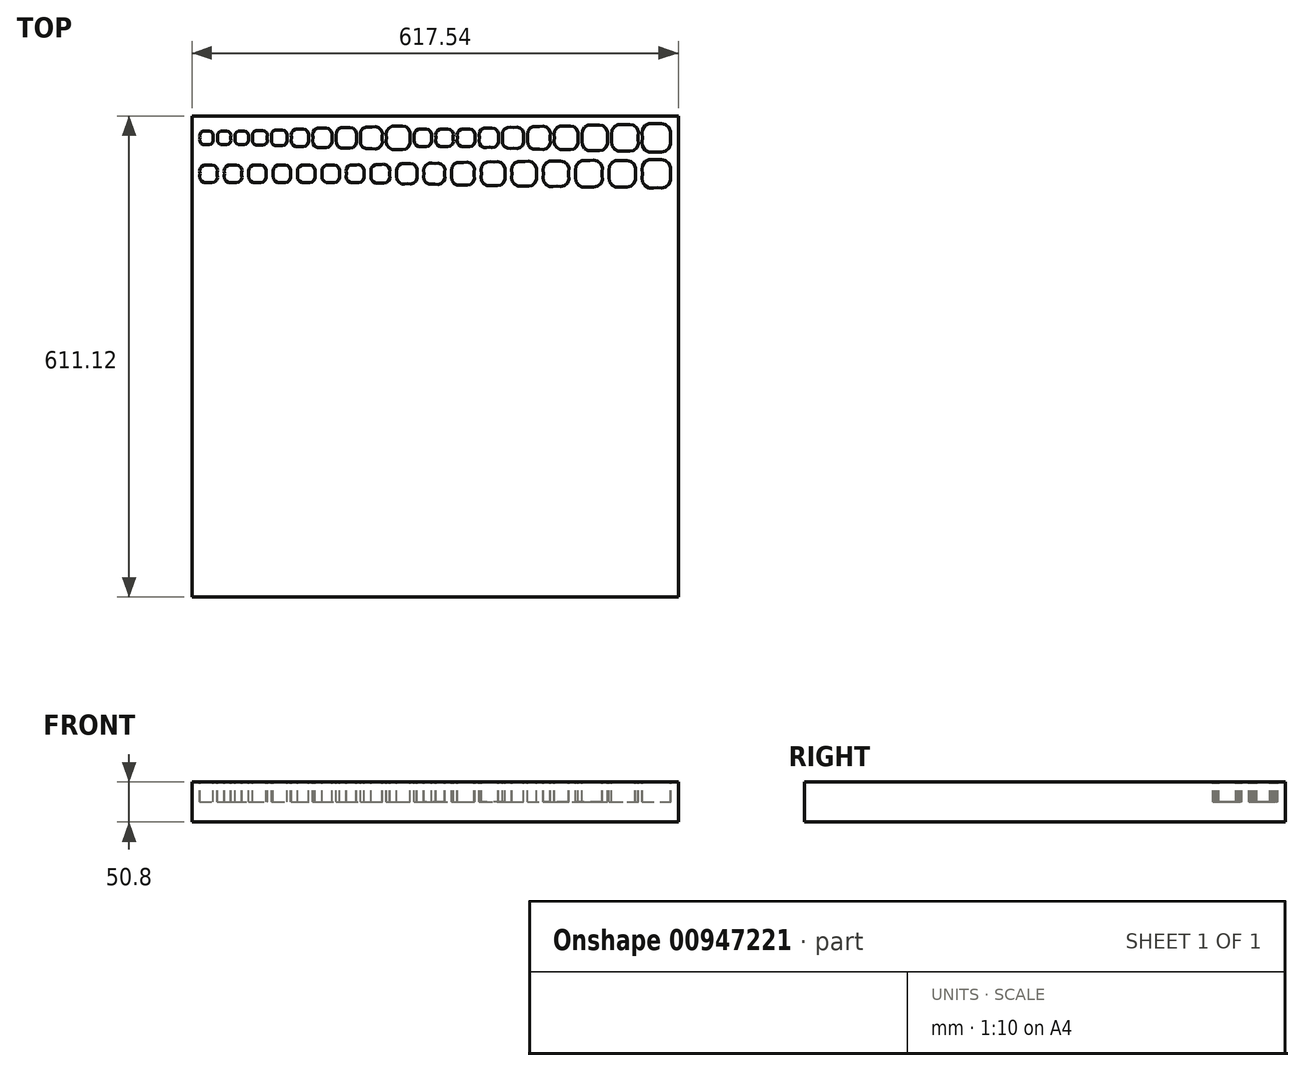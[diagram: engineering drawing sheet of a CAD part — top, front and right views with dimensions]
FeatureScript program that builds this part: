
annotation { "Feature Type Name" : "Feature", "Feature Type Description" : "" }
export const myFeature = defineFeature(function(context is Context, id is Id, definition is map)
    precondition{}
    {
        {
            var Q0;
            Q0=qCreatedBy(makeId("Top.planeOp"),FACE);
            var sketch = newSketch(context, id + "F0", { "sketchPlane" : qUnion([Q0])});
            skLineSegment(sketch, "E0", {"start": v(308.77, -305.56) * mm, "end": v(-308.77, -305.56) * mm});
            skLineSegment(sketch, "E1", {"start": v(-308.77, -305.56) * mm, "end": v(-308.77, 305.56) * mm});
            skLineSegment(sketch, "E2", {"start": v(-308.77, 305.56) * mm, "end": v(308.77, 305.56) * mm});
            skLineSegment(sketch, "E3", {"start": v(308.77, 305.56) * mm, "end": v(308.77, -305.56) * mm});
            skFitSpline(sketch, "E4", {"points": [v(263.12, 277.74) * mm, v(263.12, 287.58) * mm, v(271.1, 295.56) * mm, v(280.94, 295.56) * mm, v(290.79, 295.56) * mm, v(298.77, 287.58) * mm, v(298.77, 277.74) * mm, v(298.77, 267.9) * mm, v(290.79, 259.91) * mm, v(280.94, 259.91) * mm, v(271.1, 259.91) * mm, v(263.12, 267.9) * mm, v(263.12, 277.74) * mm]});
            skFitSpline(sketch, "E5", {"points": [v(224.2, 277.74) * mm, v(224.2, 286.96) * mm, v(231.68, 294.44) * mm, v(240.9, 294.44) * mm, v(250.13, 294.44) * mm, v(257.6, 286.96) * mm, v(257.6, 277.74) * mm, v(257.6, 268.51) * mm, v(250.13, 261.03) * mm, v(240.9, 261.03) * mm, v(231.68, 261.03) * mm, v(224.2, 268.51) * mm, v(224.2, 277.74) * mm]});
            skFitSpline(sketch, "E6", {"points": [v(186.67, 277.74) * mm, v(186.67, 286.58) * mm, v(193.84, 293.75) * mm, v(202.68, 293.75) * mm, v(211.52, 293.75) * mm, v(218.69, 286.58) * mm, v(218.69, 277.74) * mm, v(218.69, 268.9) * mm, v(211.52, 261.73) * mm, v(202.68, 261.73) * mm, v(193.84, 261.73) * mm, v(186.67, 268.9) * mm, v(186.67, 277.74) * mm]});
            skFitSpline(sketch, "E7", {"points": [v(151.47, 277.74) * mm, v(151.47, 285.94) * mm, v(158.12, 292.58) * mm, v(166.31, 292.58) * mm, v(174.51, 292.58) * mm, v(181.16, 285.94) * mm, v(181.16, 277.74) * mm, v(181.16, 269.54) * mm, v(174.51, 262.9) * mm, v(166.31, 262.9) * mm, v(158.12, 262.9) * mm, v(151.47, 269.54) * mm, v(151.47, 277.74) * mm]});
            skFitSpline(sketch, "E8", {"points": [v(117.43, 277.74) * mm, v(117.43, 285.62) * mm, v(123.82, 292) * mm, v(131.7, 292) * mm, v(139.57, 292) * mm, v(145.96, 285.62) * mm, v(145.96, 277.74) * mm, v(145.96, 269.86) * mm, v(139.57, 263.47) * mm, v(131.7, 263.47) * mm, v(123.82, 263.47) * mm, v(117.43, 269.86) * mm, v(117.43, 277.74) * mm]});
            skFitSpline(sketch, "E9", {"points": [v(85.64, 277.74) * mm, v(85.64, 285) * mm, v(91.52, 290.88) * mm, v(98.78, 290.88) * mm, v(106.04, 290.88) * mm, v(111.92, 285) * mm, v(111.92, 277.74) * mm, v(111.92, 270.48) * mm, v(106.04, 264.6) * mm, v(98.78, 264.6) * mm, v(91.52, 264.6) * mm, v(85.64, 270.48) * mm, v(85.64, 277.74) * mm]});
            skFitSpline(sketch, "E10", {"points": [v(56.07, 277.74) * mm, v(56.07, 284.38) * mm, v(61.45, 289.77) * mm, v(68.1, 289.77) * mm, v(74.74, 289.77) * mm, v(80.13, 284.38) * mm, v(80.13, 277.74) * mm, v(80.13, 271.1) * mm, v(74.74, 265.7) * mm, v(68.1, 265.7) * mm, v(61.45, 265.7) * mm, v(56.07, 271.1) * mm, v(56.07, 277.74) * mm]});
            skFitSpline(sketch, "E11", {"points": [v(28.32, 277.74) * mm, v(28.32, 283.88) * mm, v(33.3, 288.86) * mm, v(39.44, 288.86) * mm, v(45.58, 288.86) * mm, v(50.56, 283.88) * mm, v(50.56, 277.74) * mm, v(50.56, 271.6) * mm, v(45.58, 266.62) * mm, v(39.44, 266.62) * mm, v(33.3, 266.62) * mm, v(28.32, 271.6) * mm, v(28.32, 277.74) * mm]});
            skFitSpline(sketch, "E12", {"points": [v(0.8, 277.74) * mm, v(0.8, 283.81) * mm, v(5.73, 288.74) * mm, v(11.8, 288.74) * mm, v(17.88, 288.74) * mm, v(22.8, 283.81) * mm, v(22.8, 277.74) * mm, v(22.8, 271.66) * mm, v(17.88, 266.74) * mm, v(11.8, 266.74) * mm, v(5.73, 266.74) * mm, v(0.8, 271.66) * mm, v(0.8, 277.74) * mm]});
            skFitSpline(sketch, "E13", {"points": [v(-26.66, 277.74) * mm, v(-26.66, 283.8) * mm, v(-21.75, 288.72) * mm, v(-15.68, 288.72) * mm, v(-9.62, 288.72) * mm, v(-4.7, 283.8) * mm, v(-4.7, 277.74) * mm, v(-4.7, 271.67) * mm, v(-9.62, 266.76) * mm, v(-15.68, 266.76) * mm, v(-21.75, 266.76) * mm, v(-26.66, 271.67) * mm, v(-26.66, 277.74) * mm]});
            skFitSpline(sketch, "E14", {"points": [v(263.15, 232.1) * mm, v(263.15, 241.94) * mm, v(271.12, 249.91) * mm, v(280.96, 249.91) * mm, v(290.8, 249.91) * mm, v(298.77, 241.94) * mm, v(298.77, 232.1) * mm, v(298.77, 222.27) * mm, v(290.8, 214.3) * mm, v(280.96, 214.3) * mm, v(271.12, 214.3) * mm, v(263.15, 222.27) * mm, v(263.15, 232.1) * mm]});
            skFitSpline(sketch, "E15", {"points": [v(220.95, 232.1) * mm, v(220.95, 241.25) * mm, v(228.37, 248.67) * mm, v(237.52, 248.67) * mm, v(246.67, 248.67) * mm, v(254.09, 241.25) * mm, v(254.09, 232.1) * mm, v(254.09, 222.95) * mm, v(246.67, 215.53) * mm, v(237.52, 215.53) * mm, v(228.37, 215.53) * mm, v(220.95, 222.95) * mm, v(220.95, 232.1) * mm]});
            skFitSpline(sketch, "E16", {"points": [v(178.45, 232.1) * mm, v(178.45, 241.34) * mm, v(185.94, 248.82) * mm, v(195.17, 248.82) * mm, v(204.4, 248.82) * mm, v(211.9, 241.34) * mm, v(211.9, 232.1) * mm, v(211.9, 222.87) * mm, v(204.4, 215.38) * mm, v(195.17, 215.38) * mm, v(185.94, 215.38) * mm, v(178.45, 222.87) * mm, v(178.45, 232.1) * mm]});
            skFitSpline(sketch, "E17", {"points": [v(137.6, 232.1) * mm, v(137.6, 240.88) * mm, v(144.71, 248) * mm, v(153.5, 248) * mm, v(162.27, 248) * mm, v(169.4, 240.88) * mm, v(169.4, 232.1) * mm, v(169.4, 223.32) * mm, v(162.27, 216.2) * mm, v(153.5, 216.2) * mm, v(144.71, 216.2) * mm, v(137.6, 223.32) * mm, v(137.6, 232.1) * mm]});
            skFitSpline(sketch, "E18", {"points": [v(97.5, 232.1) * mm, v(97.5, 240.67) * mm, v(104.44, 247.62) * mm, v(113.01, 247.62) * mm, v(121.58, 247.62) * mm, v(128.53, 240.67) * mm, v(128.53, 232.1) * mm, v(128.53, 223.53) * mm, v(121.58, 216.58) * mm, v(113.01, 216.58) * mm, v(104.44, 216.58) * mm, v(97.5, 223.53) * mm, v(97.5, 232.1) * mm]});
            skFitSpline(sketch, "E19", {"points": [v(21, 232.1) * mm, v(21, 239.97) * mm, v(27.38, 246.36) * mm, v(35.25, 246.36) * mm, v(43.12, 246.36) * mm, v(49.5, 239.97) * mm, v(49.5, 232.1) * mm, v(49.5, 224.23) * mm, v(43.12, 217.85) * mm, v(35.25, 217.85) * mm, v(27.38, 217.85) * mm, v(21, 224.23) * mm, v(21, 232.1) * mm]});
            skFitSpline(sketch, "E20", {"points": [v(58.56, 232.1) * mm, v(58.56, 240.35) * mm, v(65.25, 247.04) * mm, v(73.5, 247.04) * mm, v(81.75, 247.04) * mm, v(88.43, 240.35) * mm, v(88.43, 232.1) * mm, v(88.43, 223.85) * mm, v(81.75, 217.17) * mm, v(73.5, 217.17) * mm, v(65.25, 217.17) * mm, v(58.56, 223.85) * mm, v(58.56, 232.1) * mm]});
            skFitSpline(sketch, "E21", {"points": [v(-14.33, 232.1) * mm, v(-14.33, 239.35) * mm, v(-8.45, 245.23) * mm, v(-1.2, 245.23) * mm, v(6.06, 245.23) * mm, v(11.93, 239.35) * mm, v(11.93, 232.1) * mm, v(11.93, 224.85) * mm, v(6.06, 218.97) * mm, v(-1.2, 218.97) * mm, v(-8.45, 218.97) * mm, v(-14.33, 224.85) * mm, v(-14.33, 232.1) * mm]});
            skFitSpline(sketch, "E22", {"points": [v(-48.8, 232.1) * mm, v(-48.8, 239.12) * mm, v(-43.1, 244.8) * mm, v(-36.09, 244.8) * mm, v(-29.07, 244.8) * mm, v(-23.38, 239.12) * mm, v(-23.38, 232.1) * mm, v(-23.38, 225.09) * mm, v(-29.07, 219.4) * mm, v(-36.09, 219.4) * mm, v(-43.1, 219.4) * mm, v(-48.8, 225.09) * mm, v(-48.8, 232.1) * mm]});
            skFitSpline(sketch, "E23", {"points": [v(-81.32, 232.1) * mm, v(-81.32, 238.58) * mm, v(-76.07, 243.84) * mm, v(-69.59, 243.84) * mm, v(-63.1, 243.84) * mm, v(-57.85, 238.58) * mm, v(-57.85, 232.1) * mm, v(-57.85, 225.62) * mm, v(-63.1, 220.37) * mm, v(-69.59, 220.37) * mm, v(-76.07, 220.37) * mm, v(-81.32, 225.62) * mm, v(-81.32, 232.1) * mm]});
            skFitSpline(sketch, "E24", {"points": [v(-112.68, 232.1) * mm, v(-112.68, 238.26) * mm, v(-107.7, 243.25) * mm, v(-101.53, 243.25) * mm, v(-95.38, 243.25) * mm, v(-90.38, 238.26) * mm, v(-90.38, 232.1) * mm, v(-90.38, 225.94) * mm, v(-95.38, 220.95) * mm, v(-101.53, 220.95) * mm, v(-107.7, 220.95) * mm, v(-112.68, 225.94) * mm, v(-112.68, 232.1) * mm]});
            skFitSpline(sketch, "E25", {"points": [v(-143.62, 232.1) * mm, v(-143.62, 238.14) * mm, v(-138.73, 243.04) * mm, v(-132.68, 243.04) * mm, v(-126.64, 243.04) * mm, v(-121.74, 238.14) * mm, v(-121.74, 232.1) * mm, v(-121.74, 226.06) * mm, v(-126.64, 221.16) * mm, v(-132.68, 221.16) * mm, v(-138.73, 221.16) * mm, v(-143.62, 226.06) * mm, v(-143.62, 232.1) * mm]});
            skFitSpline(sketch, "E26", {"points": [v(-174.68, 232.1) * mm, v(-174.68, 238.18) * mm, v(-169.76, 243.1) * mm, v(-163.68, 243.1) * mm, v(-157.6, 243.1) * mm, v(-152.68, 238.18) * mm, v(-152.68, 232.1) * mm, v(-152.68, 226.03) * mm, v(-157.6, 221.1) * mm, v(-163.68, 221.1) * mm, v(-169.76, 221.1) * mm, v(-174.68, 226.03) * mm, v(-174.68, 232.1) * mm]});
            skFitSpline(sketch, "E27", {"points": [v(-205.74, 232.1) * mm, v(-205.74, 238.18) * mm, v(-200.82, 243.1) * mm, v(-194.74, 243.1) * mm, v(-188.67, 243.1) * mm, v(-183.74, 238.18) * mm, v(-183.74, 232.1) * mm, v(-183.74, 226.03) * mm, v(-188.67, 221.1) * mm, v(-194.74, 221.1) * mm, v(-200.82, 221.1) * mm, v(-205.74, 226.03) * mm, v(-205.74, 232.1) * mm]});
            skFitSpline(sketch, "E28", {"points": [v(-236.75, 232.1) * mm, v(-236.75, 238.16) * mm, v(-231.84, 243.08) * mm, v(-225.78, 243.08) * mm, v(-219.71, 243.08) * mm, v(-214.8, 238.16) * mm, v(-214.8, 232.1) * mm, v(-214.8, 226.04) * mm, v(-219.71, 221.13) * mm, v(-225.78, 221.13) * mm, v(-231.84, 221.13) * mm, v(-236.75, 226.04) * mm, v(-236.75, 232.1) * mm]});
            skFitSpline(sketch, "E29", {"points": [v(-267.74, 232.1) * mm, v(-267.74, 238.16) * mm, v(-262.83, 243.07) * mm, v(-256.77, 243.07) * mm, v(-250.72, 243.07) * mm, v(-245.8, 238.16) * mm, v(-245.8, 232.1) * mm, v(-245.8, 226.05) * mm, v(-250.72, 221.14) * mm, v(-256.77, 221.14) * mm, v(-262.83, 221.14) * mm, v(-267.74, 226.05) * mm, v(-267.74, 232.1) * mm]});
            skFitSpline(sketch, "E30", {"points": [v(-298.77, 232.1) * mm, v(-298.77, 238.17) * mm, v(-293.85, 243.09) * mm, v(-287.78, 243.09) * mm, v(-281.72, 243.09) * mm, v(-276.8, 238.17) * mm, v(-276.8, 232.1) * mm, v(-276.8, 226.04) * mm, v(-281.72, 221.12) * mm, v(-287.78, 221.12) * mm, v(-293.85, 221.12) * mm, v(-298.77, 226.04) * mm, v(-298.77, 232.1) * mm]});
            skFitSpline(sketch, "E31", {"points": [v(-61.8, 277.74) * mm, v(-61.8, 285.92) * mm, v(-55.17, 292.55) * mm, v(-46.99, 292.55) * mm, v(-38.8, 292.55) * mm, v(-32.17, 285.92) * mm, v(-32.17, 277.74) * mm, v(-32.17, 269.55) * mm, v(-38.8, 262.92) * mm, v(-46.99, 262.92) * mm, v(-55.17, 262.92) * mm, v(-61.8, 269.55) * mm, v(-61.8, 277.74) * mm]});
            skFitSpline(sketch, "E32", {"points": [v(-94.72, 277.74) * mm, v(-94.72, 285.3) * mm, v(-88.58, 291.44) * mm, v(-81.01, 291.44) * mm, v(-73.45, 291.44) * mm, v(-67.3, 285.3) * mm, v(-67.3, 277.74) * mm, v(-67.3, 270.17) * mm, v(-73.45, 264.03) * mm, v(-81.01, 264.03) * mm, v(-88.58, 264.03) * mm, v(-94.72, 270.17) * mm, v(-94.72, 277.74) * mm]});
            skFitSpline(sketch, "E33", {"points": [v(-125.75, 277.74) * mm, v(-125.75, 284.78) * mm, v(-120.04, 290.5) * mm, v(-112.99, 290.5) * mm, v(-105.94, 290.5) * mm, v(-100.23, 284.78) * mm, v(-100.23, 277.74) * mm, v(-100.23, 270.69) * mm, v(-105.94, 264.98) * mm, v(-112.99, 264.98) * mm, v(-120.04, 264.98) * mm, v(-125.75, 270.69) * mm, v(-125.75, 277.74) * mm]});
            skFitSpline(sketch, "E34", {"points": [v(-155.4, 277.74) * mm, v(-155.4, 284.4) * mm, v(-150, 289.8) * mm, v(-143.33, 289.8) * mm, v(-136.66, 289.8) * mm, v(-131.26, 284.4) * mm, v(-131.26, 277.74) * mm, v(-131.26, 271.07) * mm, v(-136.66, 265.67) * mm, v(-143.33, 265.67) * mm, v(-150, 265.67) * mm, v(-155.4, 271.07) * mm, v(-155.4, 277.74) * mm]});
            skFitSpline(sketch, "E35", {"points": [v(-182.72, 277.74) * mm, v(-182.72, 283.76) * mm, v(-177.84, 288.64) * mm, v(-171.81, 288.64) * mm, v(-165.8, 288.64) * mm, v(-160.9, 283.76) * mm, v(-160.9, 277.74) * mm, v(-160.9, 271.71) * mm, v(-165.8, 266.83) * mm, v(-171.81, 266.83) * mm, v(-177.84, 266.83) * mm, v(-182.72, 271.71) * mm, v(-182.72, 277.74) * mm]});
            skFitSpline(sketch, "E36", {"points": [v(-207.83, 277.74) * mm, v(-207.83, 283.15) * mm, v(-203.44, 287.54) * mm, v(-198.03, 287.54) * mm, v(-192.62, 287.54) * mm, v(-188.23, 283.15) * mm, v(-188.23, 277.74) * mm, v(-188.23, 272.32) * mm, v(-192.62, 267.94) * mm, v(-198.03, 267.94) * mm, v(-203.44, 267.94) * mm, v(-207.83, 272.32) * mm, v(-207.83, 277.74) * mm]});
            skFitSpline(sketch, "E37", {"points": [v(-231.85, 277.74) * mm, v(-231.85, 282.85) * mm, v(-227.7, 287) * mm, v(-222.6, 287) * mm, v(-217.48, 287) * mm, v(-213.34, 282.85) * mm, v(-213.34, 277.74) * mm, v(-213.34, 272.63) * mm, v(-217.48, 268.48) * mm, v(-222.6, 268.48) * mm, v(-227.7, 268.48) * mm, v(-231.85, 272.63) * mm, v(-231.85, 277.74) * mm]});
            skFitSpline(sketch, "E38", {"points": [v(-254.24, 277.74) * mm, v(-254.24, 282.4) * mm, v(-250.46, 286.18) * mm, v(-245.8, 286.18) * mm, v(-241.14, 286.18) * mm, v(-237.36, 282.4) * mm, v(-237.36, 277.74) * mm, v(-237.36, 273.08) * mm, v(-241.14, 269.3) * mm, v(-245.8, 269.3) * mm, v(-250.46, 269.3) * mm, v(-254.24, 273.08) * mm, v(-254.24, 277.74) * mm]});
            skFitSpline(sketch, "E39", {"points": [v(-276.5, 277.74) * mm, v(-276.5, 282.36) * mm, v(-272.75, 286.11) * mm, v(-268.12, 286.11) * mm, v(-263.5, 286.11) * mm, v(-259.75, 282.36) * mm, v(-259.75, 277.74) * mm, v(-259.75, 273.11) * mm, v(-263.5, 269.36) * mm, v(-268.12, 269.36) * mm, v(-272.75, 269.36) * mm, v(-276.5, 273.11) * mm, v(-276.5, 277.74) * mm]});
            skFitSpline(sketch, "E40", {"points": [v(-298.77, 277.74) * mm, v(-298.77, 282.37) * mm, v(-295.02, 286.12) * mm, v(-290.39, 286.12) * mm, v(-285.76, 286.12) * mm, v(-282, 282.37) * mm, v(-282, 277.74) * mm, v(-282, 273.1) * mm, v(-285.76, 269.36) * mm, v(-290.39, 269.36) * mm, v(-295.02, 269.36) * mm, v(-298.77, 273.1) * mm, v(-298.77, 277.74) * mm]});
            skSolve(sketch);
        }
        {
            var Q0;
            Q0=makeQuery(id+"F0.imprint","IMPRINT",FACE,{"disambiguationData":[TD([[makeQuery(id+"F0.imprint","IMPRINT",EDGE,{"derivedFrom":sQuery(id+"F0.wireOp",EDGE,"E28")}),-1.0]])]});
            var Q1;
            Q1=makeQuery(id+"F0.imprint","IMPRINT",FACE,{"disambiguationData":[TD([[makeQuery(id+"F0.imprint","IMPRINT",EDGE,{"derivedFrom":sQuery(id+"F0.wireOp",EDGE,"E29")}),-1.0]])]});
            var Q2;
            Q2=makeQuery(id+"F0.imprint","IMPRINT",FACE,{"disambiguationData":[TD([[makeQuery(id+"F0.imprint","IMPRINT",EDGE,{"derivedFrom":sQuery(id+"F0.wireOp",EDGE,"E30")}),-1.0]])]});
            var Q3;
            Q3=makeQuery(id+"F0.imprint","IMPRINT",FACE,{"disambiguationData":[TD([[makeQuery(id+"F0.imprint","IMPRINT",EDGE,{"derivedFrom":sQuery(id+"F0.wireOp",EDGE,"E31")}),-1.0]])]});
            var Q4;
            Q4=makeQuery(id+"F0.imprint","IMPRINT",FACE,{"disambiguationData":[TD([[makeQuery(id+"F0.imprint","IMPRINT",EDGE,{"derivedFrom":sQuery(id+"F0.wireOp",EDGE,"E17")}),-1.0]])]});
            var Q5;
            Q5=makeQuery(id+"F0.imprint","IMPRINT",FACE,{"disambiguationData":[TD([[makeQuery(id+"F0.imprint","IMPRINT",EDGE,{"derivedFrom":sQuery(id+"F0.wireOp",EDGE,"E16")}),-1.0]])]});
            var Q6;
            Q6=makeQuery(id+"F0.imprint","IMPRINT",FACE,{"disambiguationData":[TD([[makeQuery(id+"F0.imprint","IMPRINT",EDGE,{"derivedFrom":sQuery(id+"F0.wireOp",EDGE,"E18")}),-1.0]])]});
            var Q7;
            Q7=makeQuery(id+"F0.imprint","IMPRINT",FACE,{"disambiguationData":[TD([[makeQuery(id+"F0.imprint","IMPRINT",EDGE,{"derivedFrom":sQuery(id+"F0.wireOp",EDGE,"E37")}),-1.0]])]});
            var Q8;
            Q8=makeQuery(id+"F0.imprint","IMPRINT",FACE,{"disambiguationData":[TD([[makeQuery(id+"F0.imprint","IMPRINT",EDGE,{"derivedFrom":sQuery(id+"F0.wireOp",EDGE,"E34")}),-1.0]])]});
            var Q9;
            Q9=makeQuery(id+"F0.imprint","IMPRINT",FACE,{"disambiguationData":[TD([[makeQuery(id+"F0.imprint","IMPRINT",EDGE,{"derivedFrom":sQuery(id+"F0.wireOp",EDGE,"E40")}),-1.0]])]});
            var Q10;
            Q10=makeQuery(id+"F0.imprint","IMPRINT",FACE,{"disambiguationData":[TD([[makeQuery(id+"F0.imprint","IMPRINT",EDGE,{"derivedFrom":sQuery(id+"F0.wireOp",EDGE,"E35")}),-1.0]])]});
            var Q11;
            Q11=makeQuery(id+"F0.imprint","IMPRINT",FACE,{"disambiguationData":[TD([[makeQuery(id+"F0.imprint","IMPRINT",EDGE,{"derivedFrom":sQuery(id+"F0.wireOp",EDGE,"E5")}),-1.0]])]});
            var Q12;
            Q12=makeQuery(id+"F0.imprint","IMPRINT",FACE,{"disambiguationData":[TD([[makeQuery(id+"F0.imprint","IMPRINT",EDGE,{"derivedFrom":sQuery(id+"F0.wireOp",EDGE,"E6")}),-1.0]])]});
            var Q13;
            Q13=makeQuery(id+"F0.imprint","IMPRINT",FACE,{"disambiguationData":[TD([[makeQuery(id+"F0.imprint","IMPRINT",EDGE,{"derivedFrom":sQuery(id+"F0.wireOp",EDGE,"E13")}),-1.0]])]});
            var Q14;
            Q14=makeQuery(id+"F0.imprint","IMPRINT",FACE,{"disambiguationData":[TD([[makeQuery(id+"F0.imprint","IMPRINT",EDGE,{"derivedFrom":sQuery(id+"F0.wireOp",EDGE,"E36")}),-1.0]])]});
            var Q15;
            Q15=makeQuery(id+"F0.imprint","IMPRINT",FACE,{"disambiguationData":[TD([[makeQuery(id+"F0.imprint","IMPRINT",EDGE,{"derivedFrom":sQuery(id+"F0.wireOp",EDGE,"E19")}),-1.0]])]});
            var Q16;
            Q16=makeQuery(id+"F0.imprint","IMPRINT",FACE,{"disambiguationData":[TD([[makeQuery(id+"F0.imprint","IMPRINT",EDGE,{"derivedFrom":sQuery(id+"F0.wireOp",EDGE,"E4")}),-1.0]])]});
            var Q17;
            Q17=makeQuery(id+"F0.imprint","IMPRINT",FACE,{"disambiguationData":[TD([[makeQuery(id+"F0.imprint","IMPRINT",EDGE,{"derivedFrom":sQuery(id+"F0.wireOp",EDGE,"E11")}),-1.0]])]});
            var Q18;
            Q18=makeQuery(id+"F0.imprint","IMPRINT",FACE,{"disambiguationData":[TD([[makeQuery(id+"F0.imprint","IMPRINT",EDGE,{"derivedFrom":sQuery(id+"F0.wireOp",EDGE,"E14")}),-1.0]])]});
            var Q19;
            Q19=makeQuery(id+"F0.imprint","IMPRINT",FACE,{"disambiguationData":[TD([[makeQuery(id+"F0.imprint","IMPRINT",EDGE,{"derivedFrom":sQuery(id+"F0.wireOp",EDGE,"E15")}),-1.0]])]});
            var Q20;
            Q20=makeQuery(id+"F0.imprint","IMPRINT",FACE,{"disambiguationData":[TD([[makeQuery(id+"F0.imprint","IMPRINT",EDGE,{"derivedFrom":sQuery(id+"F0.wireOp",EDGE,"E24")}),-1.0]])]});
            var Q21;
            Q21=makeQuery(id+"F0.imprint","IMPRINT",FACE,{"disambiguationData":[TD([[makeQuery(id+"F0.imprint","IMPRINT",EDGE,{"derivedFrom":sQuery(id+"F0.wireOp",EDGE,"E9")}),-1.0]])]});
            var Q22;
            Q22=makeQuery(id+"F0.imprint","IMPRINT",FACE,{"disambiguationData":[TD([[makeQuery(id+"F0.imprint","IMPRINT",EDGE,{"derivedFrom":sQuery(id+"F0.wireOp",EDGE,"E38")}),-1.0]])]});
            var Q23;
            Q23=makeQuery(id+"F0.imprint","IMPRINT",FACE,{"disambiguationData":[TD([[makeQuery(id+"F0.imprint","IMPRINT",EDGE,{"derivedFrom":sQuery(id+"F0.wireOp",EDGE,"E7")}),-1.0]])]});
            var Q24;
            Q24=makeQuery(id+"F0.imprint","IMPRINT",FACE,{"disambiguationData":[TD([[makeQuery(id+"F0.imprint","IMPRINT",EDGE,{"derivedFrom":sQuery(id+"F0.wireOp",EDGE,"E22")}),-1.0]])]});
            var Q25;
            Q25=makeQuery(id+"F0.imprint","IMPRINT",FACE,{"disambiguationData":[TD([[makeQuery(id+"F0.imprint","IMPRINT",EDGE,{"derivedFrom":sQuery(id+"F0.wireOp",EDGE,"E26")}),-1.0]])]});
            var Q26;
            Q26=makeQuery(id+"F0.imprint","IMPRINT",FACE,{"disambiguationData":[TD([[makeQuery(id+"F0.imprint","IMPRINT",EDGE,{"derivedFrom":sQuery(id+"F0.wireOp",EDGE,"E27")}),-1.0]])]});
            var Q27;
            Q27=makeQuery(id+"F0.imprint","IMPRINT",FACE,{"disambiguationData":[TD([[makeQuery(id+"F0.imprint","IMPRINT",EDGE,{"derivedFrom":sQuery(id+"F0.wireOp",EDGE,"E20")}),-1.0]])]});
            var Q28;
            Q28=makeQuery(id+"F0.imprint","IMPRINT",FACE,{"disambiguationData":[TD([[makeQuery(id+"F0.imprint","IMPRINT",EDGE,{"derivedFrom":sQuery(id+"F0.wireOp",EDGE,"E8")}),-1.0]])]});
            var Q29;
            Q29=makeQuery(id+"F0.imprint","IMPRINT",FACE,{"disambiguationData":[TD([[makeQuery(id+"F0.imprint","IMPRINT",EDGE,{"derivedFrom":sQuery(id+"F0.wireOp",EDGE,"E33")}),-1.0]])]});
            var Q30;
            Q30=makeQuery(id+"F0.imprint","IMPRINT",FACE,{"disambiguationData":[TD([[makeQuery(id+"F0.imprint","IMPRINT",EDGE,{"derivedFrom":sQuery(id+"F0.wireOp",EDGE,"E32")}),-1.0]])]});
            var Q31;
            Q31=makeQuery(id+"F0.imprint","IMPRINT",FACE,{"disambiguationData":[TD([[makeQuery(id+"F0.imprint","IMPRINT",EDGE,{"derivedFrom":sQuery(id+"F0.wireOp",EDGE,"E10")}),-1.0]])]});
            var Q32;
            Q32=makeQuery(id+"F0.imprint","IMPRINT",FACE,{"disambiguationData":[TD([[makeQuery(id+"F0.imprint","IMPRINT",EDGE,{"derivedFrom":sQuery(id+"F0.wireOp",EDGE,"E39")}),-1.0]])]});
            var Q33;
            Q33=makeQuery(id+"F0.imprint","IMPRINT",FACE,{"disambiguationData":[TD([[makeQuery(id+"F0.imprint","IMPRINT",EDGE,{"derivedFrom":sQuery(id+"F0.wireOp",EDGE,"E12")}),-1.0]])]});
            var Q34;
            Q34=makeQuery(id+"F0.imprint","IMPRINT",FACE,{"disambiguationData":[TD([[makeQuery(id+"F0.imprint","IMPRINT",EDGE,{"derivedFrom":sQuery(id+"F0.wireOp",EDGE,"E21")}),-1.0]])]});
            var Q35;
            Q35=makeQuery(id+"F0.imprint","IMPRINT",FACE,{"disambiguationData":[TD([[makeQuery(id+"F0.imprint","IMPRINT",EDGE,{"derivedFrom":sQuery(id+"F0.wireOp",EDGE,"E25")}),-1.0]])]});
            var Q36;
            Q36=makeQuery(id+"F0.imprint","IMPRINT",FACE,{"disambiguationData":[TD([[makeQuery(id+"F0.imprint","IMPRINT",EDGE,{"derivedFrom":sQuery(id+"F0.wireOp",EDGE,"E23")}),-1.0]])]});
            var Q37;
            Q37=makeQuery(id+"F0.imprint","IMPRINT",FACE,{"disambiguationData":[TD([[makeQuery(id+"F0.imprint","IMPRINT",EDGE,{"derivedFrom":sQuery(id+"F0.wireOp",EDGE,"E0")}),-1.0]])]});
            extrude(context, id + "F1", {"entities" : qUnion([Q0, Q1, Q2, Q3, Q4, Q5, Q6, Q7, Q8, Q9, Q10, Q11, Q12, Q13, Q14, Q15, Q16, Q17, Q18, Q19, Q20, Q21, Q22, Q23, Q24, Q25, Q26, Q27, Q28, Q29, Q30, Q31, Q32, Q33, Q34, Q35, Q36, Q37]), "oppositeDirection" : true, "depth" : 50.8 * mm, "offsetDistance" : 25.4 * mm});
        }
        {
            var Q0;
            Q0=makeQuery(id+"F0.imprint","IMPRINT",FACE,{"disambiguationData":[TD([[makeQuery(id+"F0.imprint","IMPRINT",EDGE,{"derivedFrom":sQuery(id+"F0.wireOp",EDGE,"E4")}),-1.0]])]});
            var Q1;
            Q1=makeQuery(id+"F0.imprint","IMPRINT",FACE,{"disambiguationData":[TD([[makeQuery(id+"F0.imprint","IMPRINT",EDGE,{"derivedFrom":sQuery(id+"F0.wireOp",EDGE,"E5")}),-1.0]])]});
            var Q2;
            Q2=makeQuery(id+"F0.imprint","IMPRINT",FACE,{"disambiguationData":[TD([[makeQuery(id+"F0.imprint","IMPRINT",EDGE,{"derivedFrom":sQuery(id+"F0.wireOp",EDGE,"E6")}),-1.0]])]});
            var Q3;
            Q3=makeQuery(id+"F0.imprint","IMPRINT",FACE,{"disambiguationData":[TD([[makeQuery(id+"F0.imprint","IMPRINT",EDGE,{"derivedFrom":sQuery(id+"F0.wireOp",EDGE,"E7")}),-1.0]])]});
            var Q4;
            Q4=makeQuery(id+"F0.imprint","IMPRINT",FACE,{"disambiguationData":[TD([[makeQuery(id+"F0.imprint","IMPRINT",EDGE,{"derivedFrom":sQuery(id+"F0.wireOp",EDGE,"E8")}),-1.0]])]});
            var Q5;
            Q5=makeQuery(id+"F0.imprint","IMPRINT",FACE,{"disambiguationData":[TD([[makeQuery(id+"F0.imprint","IMPRINT",EDGE,{"derivedFrom":sQuery(id+"F0.wireOp",EDGE,"E9")}),-1.0]])]});
            var Q6;
            Q6=makeQuery(id+"F0.imprint","IMPRINT",FACE,{"disambiguationData":[TD([[makeQuery(id+"F0.imprint","IMPRINT",EDGE,{"derivedFrom":sQuery(id+"F0.wireOp",EDGE,"E10")}),-1.0]])]});
            var Q7;
            Q7=makeQuery(id+"F0.imprint","IMPRINT",FACE,{"disambiguationData":[TD([[makeQuery(id+"F0.imprint","IMPRINT",EDGE,{"derivedFrom":sQuery(id+"F0.wireOp",EDGE,"E11")}),-1.0]])]});
            var Q8;
            Q8=makeQuery(id+"F0.imprint","IMPRINT",FACE,{"disambiguationData":[TD([[makeQuery(id+"F0.imprint","IMPRINT",EDGE,{"derivedFrom":sQuery(id+"F0.wireOp",EDGE,"E28")}),-1.0]])]});
            var Q9;
            Q9=makeQuery(id+"F0.imprint","IMPRINT",FACE,{"disambiguationData":[TD([[makeQuery(id+"F0.imprint","IMPRINT",EDGE,{"derivedFrom":sQuery(id+"F0.wireOp",EDGE,"E29")}),-1.0]])]});
            var Q10;
            Q10=makeQuery(id+"F0.imprint","IMPRINT",FACE,{"disambiguationData":[TD([[makeQuery(id+"F0.imprint","IMPRINT",EDGE,{"derivedFrom":sQuery(id+"F0.wireOp",EDGE,"E30")}),-1.0]])]});
            var Q11;
            Q11=makeQuery(id+"F0.imprint","IMPRINT",FACE,{"disambiguationData":[TD([[makeQuery(id+"F0.imprint","IMPRINT",EDGE,{"derivedFrom":sQuery(id+"F0.wireOp",EDGE,"E31")}),-1.0]])]});
            var Q12;
            Q12=makeQuery(id+"F0.imprint","IMPRINT",FACE,{"disambiguationData":[TD([[makeQuery(id+"F0.imprint","IMPRINT",EDGE,{"derivedFrom":sQuery(id+"F0.wireOp",EDGE,"E17")}),-1.0]])]});
            var Q13;
            Q13=makeQuery(id+"F0.imprint","IMPRINT",FACE,{"disambiguationData":[TD([[makeQuery(id+"F0.imprint","IMPRINT",EDGE,{"derivedFrom":sQuery(id+"F0.wireOp",EDGE,"E16")}),-1.0]])]});
            var Q14;
            Q14=makeQuery(id+"F0.imprint","IMPRINT",FACE,{"disambiguationData":[TD([[makeQuery(id+"F0.imprint","IMPRINT",EDGE,{"derivedFrom":sQuery(id+"F0.wireOp",EDGE,"E18")}),-1.0]])]});
            var Q15;
            Q15=makeQuery(id+"F0.imprint","IMPRINT",FACE,{"disambiguationData":[TD([[makeQuery(id+"F0.imprint","IMPRINT",EDGE,{"derivedFrom":sQuery(id+"F0.wireOp",EDGE,"E37")}),-1.0]])]});
            var Q16;
            Q16=makeQuery(id+"F0.imprint","IMPRINT",FACE,{"disambiguationData":[TD([[makeQuery(id+"F0.imprint","IMPRINT",EDGE,{"derivedFrom":sQuery(id+"F0.wireOp",EDGE,"E34")}),-1.0]])]});
            var Q17;
            Q17=makeQuery(id+"F0.imprint","IMPRINT",FACE,{"disambiguationData":[TD([[makeQuery(id+"F0.imprint","IMPRINT",EDGE,{"derivedFrom":sQuery(id+"F0.wireOp",EDGE,"E40")}),-1.0]])]});
            var Q18;
            Q18=makeQuery(id+"F0.imprint","IMPRINT",FACE,{"disambiguationData":[TD([[makeQuery(id+"F0.imprint","IMPRINT",EDGE,{"derivedFrom":sQuery(id+"F0.wireOp",EDGE,"E35")}),-1.0]])]});
            var Q19;
            Q19=makeQuery(id+"F0.imprint","IMPRINT",FACE,{"disambiguationData":[TD([[makeQuery(id+"F0.imprint","IMPRINT",EDGE,{"derivedFrom":sQuery(id+"F0.wireOp",EDGE,"E13")}),-1.0]])]});
            var Q20;
            Q20=makeQuery(id+"F0.imprint","IMPRINT",FACE,{"disambiguationData":[TD([[makeQuery(id+"F0.imprint","IMPRINT",EDGE,{"derivedFrom":sQuery(id+"F0.wireOp",EDGE,"E36")}),-1.0]])]});
            var Q21;
            Q21=makeQuery(id+"F0.imprint","IMPRINT",FACE,{"disambiguationData":[TD([[makeQuery(id+"F0.imprint","IMPRINT",EDGE,{"derivedFrom":sQuery(id+"F0.wireOp",EDGE,"E19")}),-1.0]])]});
            var Q22;
            Q22=makeQuery(id+"F0.imprint","IMPRINT",FACE,{"disambiguationData":[TD([[makeQuery(id+"F0.imprint","IMPRINT",EDGE,{"derivedFrom":sQuery(id+"F0.wireOp",EDGE,"E14")}),-1.0]])]});
            var Q23;
            Q23=makeQuery(id+"F0.imprint","IMPRINT",FACE,{"disambiguationData":[TD([[makeQuery(id+"F0.imprint","IMPRINT",EDGE,{"derivedFrom":sQuery(id+"F0.wireOp",EDGE,"E15")}),-1.0]])]});
            var Q24;
            Q24=makeQuery(id+"F0.imprint","IMPRINT",FACE,{"disambiguationData":[TD([[makeQuery(id+"F0.imprint","IMPRINT",EDGE,{"derivedFrom":sQuery(id+"F0.wireOp",EDGE,"E24")}),-1.0]])]});
            var Q25;
            Q25=makeQuery(id+"F0.imprint","IMPRINT",FACE,{"disambiguationData":[TD([[makeQuery(id+"F0.imprint","IMPRINT",EDGE,{"derivedFrom":sQuery(id+"F0.wireOp",EDGE,"E38")}),-1.0]])]});
            var Q26;
            Q26=makeQuery(id+"F0.imprint","IMPRINT",FACE,{"disambiguationData":[TD([[makeQuery(id+"F0.imprint","IMPRINT",EDGE,{"derivedFrom":sQuery(id+"F0.wireOp",EDGE,"E22")}),-1.0]])]});
            var Q27;
            Q27=makeQuery(id+"F0.imprint","IMPRINT",FACE,{"disambiguationData":[TD([[makeQuery(id+"F0.imprint","IMPRINT",EDGE,{"derivedFrom":sQuery(id+"F0.wireOp",EDGE,"E26")}),-1.0]])]});
            var Q28;
            Q28=makeQuery(id+"F0.imprint","IMPRINT",FACE,{"disambiguationData":[TD([[makeQuery(id+"F0.imprint","IMPRINT",EDGE,{"derivedFrom":sQuery(id+"F0.wireOp",EDGE,"E27")}),-1.0]])]});
            var Q29;
            Q29=makeQuery(id+"F0.imprint","IMPRINT",FACE,{"disambiguationData":[TD([[makeQuery(id+"F0.imprint","IMPRINT",EDGE,{"derivedFrom":sQuery(id+"F0.wireOp",EDGE,"E20")}),-1.0]])]});
            var Q30;
            Q30=makeQuery(id+"F0.imprint","IMPRINT",FACE,{"disambiguationData":[TD([[makeQuery(id+"F0.imprint","IMPRINT",EDGE,{"derivedFrom":sQuery(id+"F0.wireOp",EDGE,"E33")}),-1.0]])]});
            var Q31;
            Q31=makeQuery(id+"F0.imprint","IMPRINT",FACE,{"disambiguationData":[TD([[makeQuery(id+"F0.imprint","IMPRINT",EDGE,{"derivedFrom":sQuery(id+"F0.wireOp",EDGE,"E32")}),-1.0]])]});
            var Q32;
            Q32=makeQuery(id+"F0.imprint","IMPRINT",FACE,{"disambiguationData":[TD([[makeQuery(id+"F0.imprint","IMPRINT",EDGE,{"derivedFrom":sQuery(id+"F0.wireOp",EDGE,"E39")}),-1.0]])]});
            var Q33;
            Q33=makeQuery(id+"F0.imprint","IMPRINT",FACE,{"disambiguationData":[TD([[makeQuery(id+"F0.imprint","IMPRINT",EDGE,{"derivedFrom":sQuery(id+"F0.wireOp",EDGE,"E12")}),-1.0]])]});
            var Q34;
            Q34=makeQuery(id+"F0.imprint","IMPRINT",FACE,{"disambiguationData":[TD([[makeQuery(id+"F0.imprint","IMPRINT",EDGE,{"derivedFrom":sQuery(id+"F0.wireOp",EDGE,"E21")}),-1.0]])]});
            var Q35;
            Q35=makeQuery(id+"F0.imprint","IMPRINT",FACE,{"disambiguationData":[TD([[makeQuery(id+"F0.imprint","IMPRINT",EDGE,{"derivedFrom":sQuery(id+"F0.wireOp",EDGE,"E25")}),-1.0]])]});
            var Q36;
            Q36=makeQuery(id+"F0.imprint","IMPRINT",FACE,{"disambiguationData":[TD([[makeQuery(id+"F0.imprint","IMPRINT",EDGE,{"derivedFrom":sQuery(id+"F0.wireOp",EDGE,"E23")}),-1.0]])]});
            extrude(context, id + "F2", {"entities" : qUnion([Q0, Q1, Q2, Q3, Q4, Q5, Q6, Q7, Q8, Q9, Q10, Q11, Q12, Q13, Q14, Q15, Q16, Q17, Q18, Q19, Q20, Q21, Q22, Q23, Q24, Q25, Q26, Q27, Q28, Q29, Q30, Q31, Q32, Q33, Q34, Q35, Q36]), "operationType" : NewBodyOperationType.REMOVE, "oppositeDirection" : true, "depth" : 25.4 * mm, "offsetDistance" : 25.4 * mm});
        }
    });
